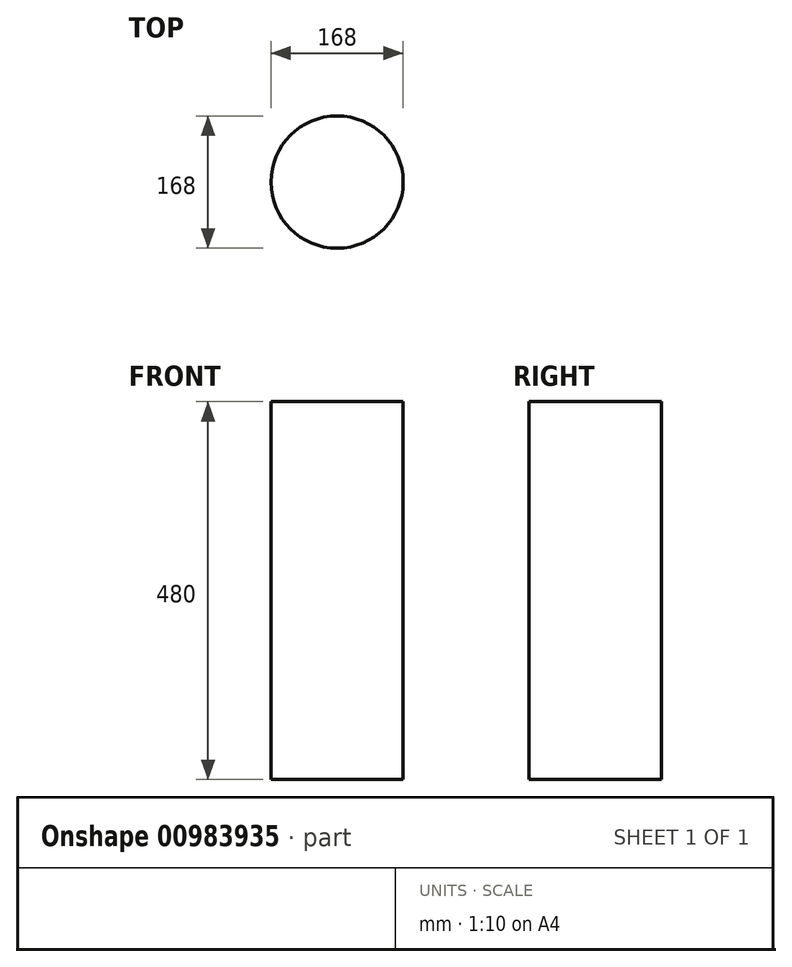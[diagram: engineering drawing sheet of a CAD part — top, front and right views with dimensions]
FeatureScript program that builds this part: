
annotation { "Feature Type Name" : "Feature", "Feature Type Description" : "" }
export const myFeature = defineFeature(function(context is Context, id is Id, definition is map)
    precondition{}
    {
        {
            var Q0;
            Q0=qCreatedBy(makeId("Top.planeOp"),FACE);
            var sketch = newSketch(context, id + "F0", { "sketchPlane" : qUnion([Q0])});
            skCircle(sketch, "E0", {"center": v(0, 0) * mm, "radius": 84 * mm});
            skSolve(sketch);
        }
        {
            var Q0;
            Q0=makeQuery(id+"F0.imprint","IMPRINT",FACE,{"disambiguationData":[TD([[makeQuery(id+"F0.imprint","IMPRINT",EDGE,{"derivedFrom":sQuery(id+"F0.wireOp",EDGE,"E0")}),1.0]])]});
            extrude(context, id + "F1", {"entities" : qUnion([Q0]), "depth" : 480 * mm, "offsetDistance" : 25 * mm});
        }
    });
